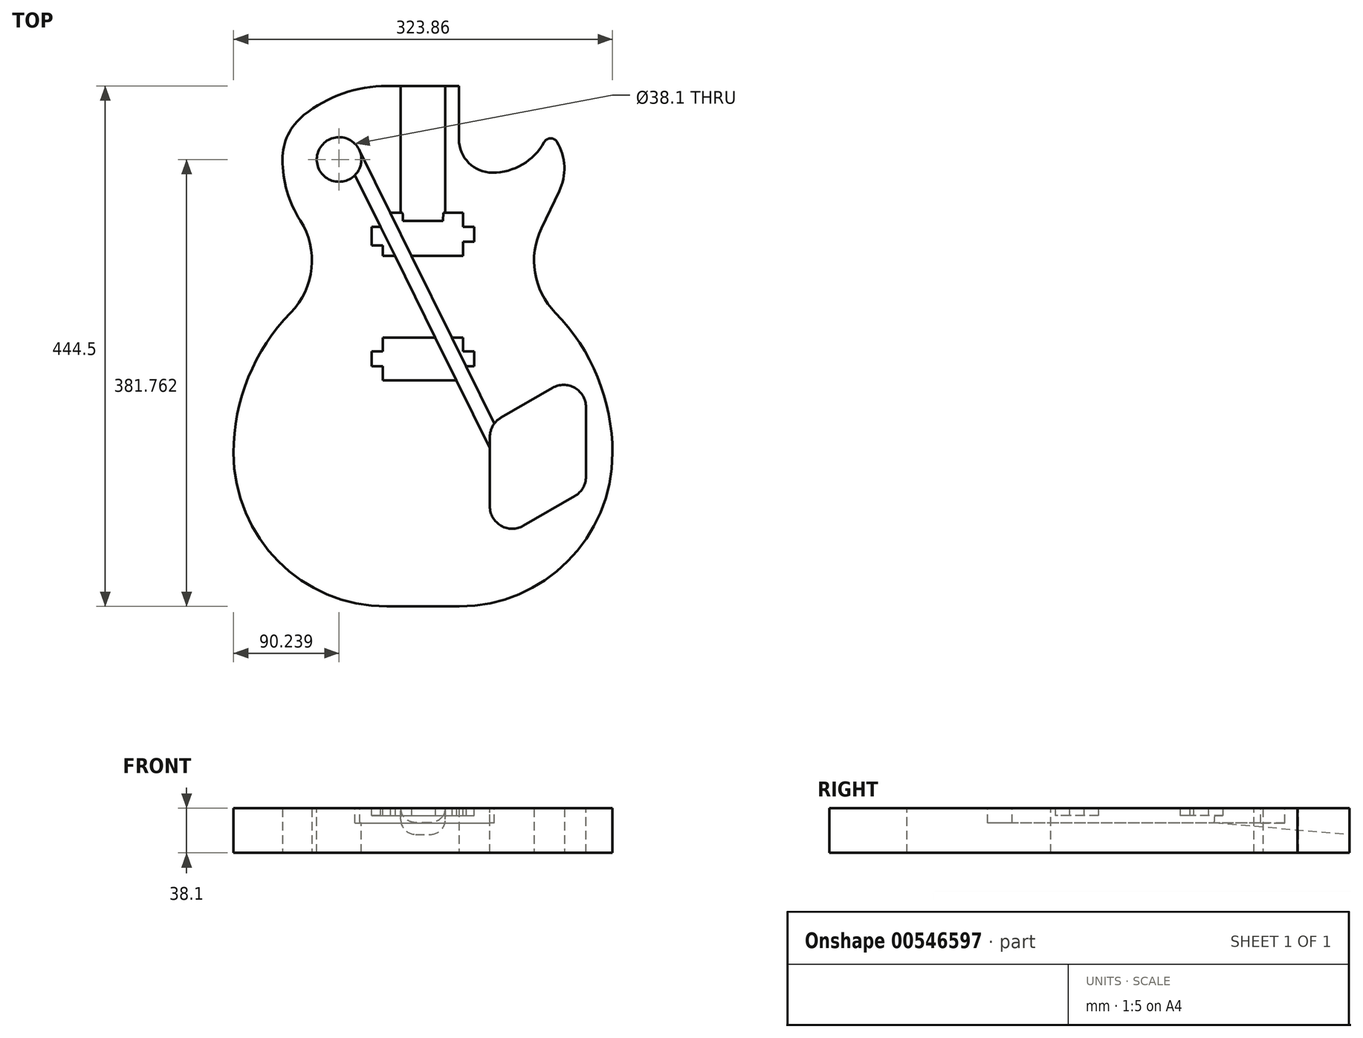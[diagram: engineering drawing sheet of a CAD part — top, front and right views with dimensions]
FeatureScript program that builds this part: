
annotation { "Feature Type Name" : "Feature", "Feature Type Description" : "" }
export const myFeature = defineFeature(function(context is Context, id is Id, definition is map)
    precondition{}
    {
        {
            var Q0;
            Q0=qCreatedBy(makeId("Top.planeOp"),FACE);
            var sketch = newSketch(context, id + "F0", { "sketchPlane" : qUnion([Q0])});
            skLineSegment(sketch, "E0.bottom", {"start": v(-161.92, 444.5) * mm, "end": v(161.92, 444.5) * mm});
            skLineSegment(sketch, "E0.top", {"start": v(-161.93, 0) * mm, "end": v(161.93, 0) * mm});
            skLineSegment(sketch, "E0.left", {"start": v(-161.92, 444.5) * mm, "end": v(-161.93, 0) * mm});
            skLineSegment(sketch, "E0.right", {"start": v(161.93, 444.5) * mm, "end": v(161.93, 0) * mm});
            skSolve(sketch);
        }
        {
            var Q0;
            Q0=qCreatedBy(makeId("Top.planeOp"),FACE);
            var sketch = newSketch(context, id + "F1", { "sketchPlane" : qUnion([Q0])});
            skLineSegment(sketch, "E1", {"start": v(-94.87, 295.4) * mm, "end": v(94.87, 295.4) * mm});
            skLineSegment(sketch, "E2", {"start": v(0, 0) * mm, "end": v(0, 295.4) * mm});
            skArc(sketch, "E3", {"start": v(-161.92, 131.02) * mm, "mid": v(-123.55, 38.37) * mm, "end": v(-30.9, 0) * mm});
            skLineSegment(sketch, "E4", {"start": v(-30.9, 0) * mm, "end": v(0, 0) * mm});
            skArc(sketch, "E5", {"start": v(-112.99, 250.99) * mm, "mid": v(-95.2, 288.9) * mm, "end": v(-104.89, 329.64) * mm});
            skLineSegment(sketch, "E6", {"start": v(-94.87, 295.4) * mm, "end": v(-94.87, 252.93) * mm});
            skLineSegment(sketch, "E7", {"start": v(-120.14, 381.76) * mm, "end": v(120.14, 381.76) * mm});
            skLineSegment(sketch, "E8", {"start": v(0, 295.4) * mm, "end": v(0, 381.76) * mm});
            skLineSegment(sketch, "E9", {"start": v(-120.14, 381.76) * mm, "end": v(-120.14, 343.59) * mm});
            skLineSegment(sketch, "E10", {"start": v(0, 381.76) * mm, "end": v(0, 444.5) * mm});
            skLineSegment(sketch, "E11", {"start": v(0, 444.5) * mm, "end": v(-30.73, 444.5) * mm});
            skArc(sketch, "E12", {"start": v(-112.99, 250.99) * mm, "mid": v(-149.22, 195.8) * mm, "end": v(-161.93, 131.02) * mm});
            skArc(sketch, "E13", {"start": v(-120.14, 381.76) * mm, "mid": v(-116.25, 354.6) * mm, "end": v(-104.89, 329.64) * mm});
            skArc(sketch, "E14", {"start": v(-101.83, 419.7) * mm, "mid": v(-115.32, 402.83) * mm, "end": v(-120.14, 381.76) * mm});
            skArc(sketch, "E15", {"start": v(-30.73, 444.5) * mm, "mid": v(-68.38, 438.12) * mm, "end": v(-101.83, 419.7) * mm});
            skLineSegment(sketch, "E16.MirrorCS", {"start": v(30.9, 0) * mm, "end": v(0, 0) * mm});
            skArc(sketch, "E17.MirrorCS", {"start": v(161.92, 131.02) * mm, "mid": v(123.55, 38.37) * mm, "end": v(30.9, 0) * mm});
            skArc(sketch, "E18.MirrorCS", {"start": v(112.99, 250.99) * mm, "mid": v(149.22, 195.8) * mm, "end": v(161.93, 131.02) * mm});
            skLineSegment(sketch, "E19", {"start": v(80.77, 399.8) * mm, "end": v(130.06, 399.8) * mm});
            skLineSegment(sketch, "E20", {"start": v(0, 444.5) * mm, "end": v(30.73, 444.5) * mm});
            skLineSegment(sketch, "E21", {"start": v(30.73, 444.5) * mm, "end": v(30.73, 399.03) * mm});
            skArc(sketch, "E22", {"start": v(30.73, 399.03) * mm, "mid": v(39.1, 378.83) * mm, "end": v(59.3, 370.46) * mm});
            skArc(sketch, "E23", {"start": v(101.18, 323) * mm, "mid": v(95.7, 285.13) * mm, "end": v(112.99, 250.99) * mm});
            skLineSegment(sketch, "E24", {"start": v(101.18, 323) * mm, "end": v(116.42, 354.6) * mm});
            skArc(sketch, "E25", {"start": v(116.42, 354.6) * mm, "mid": v(120.8, 375.88) * mm, "end": v(114.55, 396.7) * mm});
            skLineSegment(sketch, "E26", {"start": v(26.22, 370.46) * mm, "end": v(78.39, 370.46) * mm});
            skArc(sketch, "E27", {"start": v(114.55, 396.7) * mm, "mid": v(109, 399.8) * mm, "end": v(103.55, 396.52) * mm});
            skArc(sketch, "E28", {"start": v(59.3, 370.46) * mm, "mid": v(84.98, 377.46) * mm, "end": v(103.55, 396.52) * mm});
            skSolve(sketch);
        }
        {
            var Q0;
            {var subQ1=sQuery(id+"F1.wireOp",EDGE,"E10");Q0=makeQuery(id+"F1.imprint","IMPRINT",FACE,{"disambiguationData":[TD([[makeQuery(id+"F1.imprint","IMPRINT",EDGE,{"derivedFrom":subQ1}),1.0]])]});}
            var Q1;
            {var subQ1=sQuery(id+"F1.wireOp",EDGE,"E10");Q1=makeQuery(id+"F1.imprint","IMPRINT",FACE,{"disambiguationData":[TD([[makeQuery(id+"F1.imprint","IMPRINT",EDGE,{"derivedFrom":subQ1}),-1.0]])]});}
            var Q2;
            {var subQ5=sQuery(id+"F1.wireOp",EDGE,"E8");Q2=makeQuery(id+"F1.imprint","IMPRINT",FACE,{"disambiguationData":[TD([[makeQuery(id+"F1.imprint","IMPRINT",EDGE,{"derivedFrom":subQ5}),-1.0]])]});}
            var Q3;
            {var subQ0=sQuery(id+"F1.wireOp",EDGE,"E25");var subQ1=sQuery(id+"F1.wireOp",EDGE,"E7");var subQ2=makeQuery(id+"F1.imprint","INTERSECT",VERTEX,{"derivedFrom":[subQ1,subQ0]});Q3=makeQuery(id+"F1.imprint","IMPRINT",FACE,{"disambiguationData":[TD([[makeQuery(id+"F1.imprint","IMPRINT",EDGE,{"disambiguationData":[TD([[subQ2,1.0]])],"derivedFrom":subQ1}),1.0]])]});}
            var Q4;
            {var subQ0=sQuery(id+"F1.wireOp",EDGE,"E2");Q4=makeQuery(id+"F1.imprint","IMPRINT",FACE,{"disambiguationData":[TD([[makeQuery(id+"F1.imprint","IMPRINT",EDGE,{"derivedFrom":subQ0}),-1.0]])]});}
            var Q5;
            {var subQ1=sQuery(id+"F1.wireOp",EDGE,"E2");Q5=makeQuery(id+"F1.imprint","IMPRINT",FACE,{"disambiguationData":[TD([[makeQuery(id+"F1.imprint","IMPRINT",EDGE,{"derivedFrom":subQ1}),1.0]])]});}
            var Q6;
            {var subQ2=sQuery(id+"F1.wireOp",EDGE,"E8");Q6=makeQuery(id+"F1.imprint","IMPRINT",FACE,{"disambiguationData":[TD([[makeQuery(id+"F1.imprint","IMPRINT",EDGE,{"derivedFrom":subQ2}),1.0]])]});}
            extrude(context, id + "F2", {"entities" : qUnion([Q0, Q1, Q2, Q3, Q4, Q5, Q6]), "depth" : 38.1 * mm});
        }
        {
            var Q0;
            Q0=makeQuery(id+"F2.opExtrude","CAP_FACE",FACE,{"disambiguationData":[OSD([sQuery(id+"F1.wireOp",EDGE,"E3"),sQuery(id+"F1.wireOp",EDGE,"E4"),sQuery(id+"F1.wireOp",EDGE,"E5"),sQuery(id+"F1.wireOp",EDGE,"E11"),sQuery(id+"F1.wireOp",EDGE,"E12"),sQuery(id+"F1.wireOp",EDGE,"E13"),sQuery(id+"F1.wireOp",EDGE,"E14"),sQuery(id+"F1.wireOp",EDGE,"E15"),sQuery(id+"F1.wireOp",EDGE,"E16.MirrorCS"),sQuery(id+"F1.wireOp",EDGE,"E17.MirrorCS"),sQuery(id+"F1.wireOp",EDGE,"E18.MirrorCS"),sQuery(id+"F1.wireOp",EDGE,"E20"),sQuery(id+"F1.wireOp",EDGE,"E21"),sQuery(id+"F1.wireOp",EDGE,"E22"),sQuery(id+"F1.wireOp",EDGE,"E23"),sQuery(id+"F1.wireOp",EDGE,"E24"),sQuery(id+"F1.wireOp",EDGE,"E25"),sQuery(id+"F1.wireOp",EDGE,"E27"),sQuery(id+"F1.wireOp",EDGE,"E28")])],"isStart":false});
            var sketch = newSketch(context, id + "F3", { "sketchPlane" : qUnion([Q0])});
            skCircle(sketch, "E29", {"center": v(120.25, 170.1) * mm, "radius": 14.29 * mm});
            skCircle(sketch, "E30", {"center": v(76.2, 144.67) * mm, "radius": 14.29 * mm});
            skCircle(sketch, "E31", {"center": v(120.25, 110.8) * mm, "radius": 14.29 * mm});
            skCircle(sketch, "E32", {"center": v(76.2, 85.37) * mm, "radius": 14.29 * mm});
            skLineSegment(sketch, "E33", {"start": v(0, 0) * mm, "end": v(76.2, 144.67) * mm});
            skLineSegment(sketch, "E34", {"start": v(0, 0) * mm, "end": v(120.25, 110.8) * mm});
            skLineSegment(sketch, "E35", {"start": v(0, 0) * mm, "end": v(0, 365.77) * mm});
            skLineSegment(sketch, "E36", {"start": v(76.2, 144.67) * mm, "end": v(120.25, 110.8) * mm});
            skLineSegment(sketch, "E37", {"start": v(76.2, 144.67) * mm, "end": v(76.2, 85.37) * mm});
            skLineSegment(sketch, "E38", {"start": v(120.25, 110.8) * mm, "end": v(76.2, 85.37) * mm});
            skLineSegment(sketch, "E39", {"start": v(76.2, 144.67) * mm, "end": v(120.25, 170.1) * mm});
            skLineSegment(sketch, "E40", {"start": v(120.25, 110.8) * mm, "end": v(120.25, 170.1) * mm});
            skCircle(sketch, "E41", {"center": v(-71.7, 381.76) * mm, "radius": 19.05 * mm});
            skSolve(sketch);
        }
        {
            var Q0;
            Q0=makeQuery(id+"F3.imprint","IMPRINT",FACE,{"disambiguationData":[TD([[makeQuery(id+"F3.imprint","IMPRINT",EDGE,{"derivedFrom":sQuery(id+"F3.wireOp",EDGE,"E41")}),-1.0]])]});
            var sketch = newSketch(context, id + "F4", { "sketchPlane" : qUnion([Q0])});
            skCircle(sketch, "E42", {"center": v(-71.7, 381.76) * mm, "radius": 19.05 * mm});
            skArc(sketch, "E43", {"start": v(139.3, 170.1) * mm, "mid": v(129.77, 186.6) * mm, "end": v(110.72, 186.6) * mm});
            skArc(sketch, "E44", {"start": v(129.77, 94.3) * mm, "mid": v(136.74, 101.28) * mm, "end": v(139.3, 110.8) * mm});
            skArc(sketch, "E45", {"start": v(57.15, 85.37) * mm, "mid": v(66.67, 68.87) * mm, "end": v(85.72, 68.87) * mm});
            skArc(sketch, "E46", {"start": v(66.67, 161.17) * mm, "mid": v(59.7, 154.2) * mm, "end": v(57.15, 144.67) * mm});
            skLineSegment(sketch, "E47", {"start": v(110.72, 186.6) * mm, "end": v(66.68, 161.17) * mm});
            skLineSegment(sketch, "E48", {"start": v(57.15, 144.67) * mm, "end": v(57.15, 85.37) * mm});
            skLineSegment(sketch, "E49", {"start": v(85.72, 68.87) * mm, "end": v(129.77, 94.3) * mm});
            skLineSegment(sketch, "E50", {"start": v(139.3, 110.8) * mm, "end": v(139.3, 170.1) * mm});
            skSolve(sketch);
        }
        {
            var Q0;
            Q0=makeQuery(id+"F4.imprint","IMPRINT",FACE,{"disambiguationData":[TD([[makeQuery(id+"F4.imprint","IMPRINT",EDGE,{"derivedFrom":sQuery(id+"F4.wireOp",EDGE,"E42")}),1.0]])]});
            var Q1;
            Q1=makeQuery(id+"F4.imprint","IMPRINT",FACE,{"disambiguationData":[TD([[makeQuery(id+"F4.imprint","IMPRINT",EDGE,{"derivedFrom":sQuery(id+"F4.wireOp",EDGE,"E43")}),1.0]])]});
            var Q2;
            {var subQ1=sQuery(id+"F3.wireOp",EDGE,"E29");var subQ5=sQuery(id+"F3.wireOp",EDGE,"E39");var subQ6=makeQuery(id+"F3.imprint","INTERSECT",VERTEX,{"derivedFrom":[subQ1,subQ5]});Q2=makeQuery(id+"F4.imprint","IMPRINT",FACE,{"disambiguationData":[TD([[makeQuery(id+"F4.imprint","IMPRINT",EDGE,{"derivedFrom":makeQuery(id+"F3.imprint","IMPRINT",EDGE,{"disambiguationData":[TD([[subQ6,1.0]])],"derivedFrom":subQ1})}),1.0]])]});}
            extrude(context, id + "F5", {"entities" : qUnion([Q0, Q1, Q2]), "operationType" : NewBodyOperationType.REMOVE, "endBound" : BoundingType.THROUGH_ALL, "oppositeDirection" : true, "depth" : 25.4 * mm});
        }
        {
            var Q0;
            Q0=makeQuery(id+"F2.opExtrude","CAP_FACE",FACE,{"disambiguationData":[OSD([sQuery(id+"F1.wireOp",EDGE,"E3"),sQuery(id+"F1.wireOp",EDGE,"E4"),sQuery(id+"F1.wireOp",EDGE,"E5"),sQuery(id+"F1.wireOp",EDGE,"E11"),sQuery(id+"F1.wireOp",EDGE,"E12"),sQuery(id+"F1.wireOp",EDGE,"E13"),sQuery(id+"F1.wireOp",EDGE,"E14"),sQuery(id+"F1.wireOp",EDGE,"E15"),sQuery(id+"F1.wireOp",EDGE,"E16.MirrorCS"),sQuery(id+"F1.wireOp",EDGE,"E17.MirrorCS"),sQuery(id+"F1.wireOp",EDGE,"E18.MirrorCS"),sQuery(id+"F1.wireOp",EDGE,"E20"),sQuery(id+"F1.wireOp",EDGE,"E21"),sQuery(id+"F1.wireOp",EDGE,"E22"),sQuery(id+"F1.wireOp",EDGE,"E23"),sQuery(id+"F1.wireOp",EDGE,"E24"),sQuery(id+"F1.wireOp",EDGE,"E25"),sQuery(id+"F1.wireOp",EDGE,"E27"),sQuery(id+"F1.wireOp",EDGE,"E28")])],"isStart":false});
            var sketch = newSketch(context, id + "F6", { "sketchPlane" : qUnion([Q0])});
            skArc(sketch, "E51", {"start": v(-69.5, 374.93) * mm, "mid": v(-78.43, 375.8) * mm, "end": v(-79.3, 366.85) * mm});
            skArc(sketch, "E52", {"start": v(90.35, 161.06) * mm, "mid": v(99.29, 160.2) * mm, "end": v(100.15, 169.14) * mm});
            skLineSegment(sketch, "E53", {"start": v(90.35, 161.06) * mm, "end": v(-79.3, 366.85) * mm});
            skLineSegment(sketch, "E54", {"start": v(-69.5, 374.93) * mm, "end": v(100.15, 169.14) * mm});
            skLineSegment(sketch, "E55", {"start": v(0, 0) * mm, "end": v(0, 165.1) * mm});
            skLineSegment(sketch, "E56", {"start": v(0, 165.1) * mm, "end": v(95.25, 165.1) * mm});
            skSolve(sketch);
        }
        {
            var Q0;
            {var subQ0=sQuery(id+"F6.wireOp",EDGE,"E53");var subQ1=makeQuery(id+"F5.boolean.opBoolean","COPY",EDGE,{"derivedFrom":makeQuery(id+"F5.opExtrude","CAP_EDGE",EDGE,{"disambiguationData":[OSD([sQuery(id+"F4.wireOp",EDGE,"MkLr8Pz1-1iLs-kMEC-wIaN-vfKRpLqlfBYC")])],"isStart":true})});var subQ2=makeQuery(id+"F6.imprint","INTERSECT",VERTEX,{"derivedFrom":[subQ1,subQ0]});Q0=makeQuery(id+"F6.imprint","IMPRINT",FACE,{"disambiguationData":[TD([[makeQuery(id+"F6.imprint","IMPRINT",EDGE,{"disambiguationData":[TD([[subQ2,-1.0]])],"derivedFrom":subQ0}),-1.0]])]});}
            extrude(context, id + "F7", {"entities" : qUnion([Q0]), "operationType" : NewBodyOperationType.REMOVE, "oppositeDirection" : true, "depth" : 12.7 * mm});
        }
        {
            var Q0;
            Q0=makeQuery(id+"F2.opExtrude","SWEPT_FACE",FACE,{"disambiguationData":[OSD([sQuery(id+"F1.wireOp",EDGE,"E21")])]});
            var sketch = newSketch(context, id + "F8", { "sketchPlane" : qUnion([Q0])});
            skLineSegment(sketch, "E57", {"start": v(444.5, 0) * mm, "end": v(451.24, 77) * mm});
            skSolve(sketch);
        }
        {
            var Q0;
            Q0=makeQuery(id+"F2.opExtrude","CAP_EDGE",EDGE,{"disambiguationData":[OSD([sQuery(id+"F1.wireOp",EDGE,"E11"),sQuery(id+"F1.wireOp",EDGE,"E20")])],"isStart":true});
            var Q1;
            Q1=sQuery(id+"F8.wireOp",EDGE,"E57");
            cPlane(context, id + "F9", {"entities" : qUnion([Q0, Q1]), "cplaneType" : CPlaneType.LINE_ANGLE, "offset" : 25.4 * mm, "angle" : 0 * degree, "width" : 152.4 * mm, "height" : 152.4 * mm});
        }
        {
            var Q0;
            Q0=qCreatedBy(id+"F9.planeOp",FACE);
            var sketch = newSketch(context, id + "F10", { "sketchPlane" : qUnion([Q0])});
            skLineSegment(sketch, "E58", {"start": v(-19.05, 76.7) * mm, "end": v(19.05, 76.7) * mm});
            skLineSegment(sketch, "E59", {"start": v(19.05, 76.7) * mm, "end": v(19.05, 67.17) * mm});
            skLineSegment(sketch, "E60", {"start": v(-19.05, 76.7) * mm, "end": v(-19.05, 67.17) * mm});
            skLineSegment(sketch, "E61", {"start": v(-6.35, 54.47) * mm, "end": v(6.35, 54.47) * mm});
            skArc(sketch, "E62", {"start": v(-19.05, 67.17) * mm, "mid": v(-15.33, 58.2) * mm, "end": v(-6.35, 54.47) * mm});
            skArc(sketch, "E63", {"start": v(6.35, 54.47) * mm, "mid": v(15.33, 58.2) * mm, "end": v(19.05, 67.17) * mm});
            skLineSegment(sketch, "E64", {"start": v(0, 38.74) * mm, "end": v(0, 54.47) * mm});
            skSolve(sketch);
        }
        {
            var Q0;
            Q0=qSketchRegion(id+"F10",true);
            extrude(context, id + "F11", {"entities" : qUnion([Q0]), "operationType" : NewBodyOperationType.REMOVE, "oppositeDirection" : true, "depth" : 117.47 * mm});
        }
        {
            var Q0;
            Q0=makeQuery(id+"F2.opExtrude","CAP_FACE",FACE,{"disambiguationData":[OSD([sQuery(id+"F1.wireOp",EDGE,"E3"),sQuery(id+"F1.wireOp",EDGE,"E4"),sQuery(id+"F1.wireOp",EDGE,"E5"),sQuery(id+"F1.wireOp",EDGE,"E11"),sQuery(id+"F1.wireOp",EDGE,"E12"),sQuery(id+"F1.wireOp",EDGE,"E13"),sQuery(id+"F1.wireOp",EDGE,"E14"),sQuery(id+"F1.wireOp",EDGE,"E15"),sQuery(id+"F1.wireOp",EDGE,"E16.MirrorCS"),sQuery(id+"F1.wireOp",EDGE,"E17.MirrorCS"),sQuery(id+"F1.wireOp",EDGE,"E18.MirrorCS"),sQuery(id+"F1.wireOp",EDGE,"E20"),sQuery(id+"F1.wireOp",EDGE,"E21"),sQuery(id+"F1.wireOp",EDGE,"E22"),sQuery(id+"F1.wireOp",EDGE,"E23"),sQuery(id+"F1.wireOp",EDGE,"E24"),sQuery(id+"F1.wireOp",EDGE,"E25"),sQuery(id+"F1.wireOp",EDGE,"E27"),sQuery(id+"F1.wireOp",EDGE,"E28")])],"isStart":false});
            var sketch = newSketch(context, id + "F12", { "sketchPlane" : qUnion([Q0])});
            skLineSegment(sketch, "E65.bottom", {"start": v(-34.3, 229.67) * mm, "end": v(34.3, 229.67) * mm});
            skLineSegment(sketch, "E65.top", {"start": v(-34.3, 193.04) * mm, "end": v(34.29, 193.04) * mm});
            skLineSegment(sketch, "E65.left", {"start": v(-34.3, 229.67) * mm, "end": v(-34.3, 193.04) * mm});
            skLineSegment(sketch, "E65.right", {"start": v(34.3, 229.67) * mm, "end": v(34.3, 193.04) * mm});
            skLineSegment(sketch, "E66.bottom", {"start": v(-34.3, 336.14) * mm, "end": v(34.29, 336.14) * mm});
            skLineSegment(sketch, "E66.top", {"start": v(-34.3, 299.52) * mm, "end": v(34.29, 299.52) * mm});
            skLineSegment(sketch, "E66.left", {"start": v(-34.3, 336.14) * mm, "end": v(-34.3, 299.52) * mm});
            skLineSegment(sketch, "E66.right", {"start": v(34.29, 336.14) * mm, "end": v(34.29, 299.52) * mm});
            skLineSegment(sketch, "E67", {"start": v(0, 444.5) * mm, "end": v(0, 336.14) * mm});
            skLineSegment(sketch, "E68", {"start": v(0, 299.52) * mm, "end": v(0, 229.67) * mm});
            skLineSegment(sketch, "E69", {"start": v(0, 229.67) * mm, "end": v(0, 211.35) * mm});
            skLineSegment(sketch, "E70", {"start": v(0, 211.35) * mm, "end": v(0, 193.04) * mm});
            skLineSegment(sketch, "E71.bottom", {"start": v(-34.3, 324.18) * mm, "end": v(-43.82, 324.18) * mm});
            skLineSegment(sketch, "E71.left", {"start": v(-34.3, 324.18) * mm, "end": v(-34.3, 311.48) * mm});
            skLineSegment(sketch, "E71.right", {"start": v(-43.82, 324.18) * mm, "end": v(-43.82, 311.48) * mm});
            skLineSegment(sketch, "E72.bottom", {"start": v(34.29, 324.18) * mm, "end": v(43.81, 324.18) * mm});
            skLineSegment(sketch, "E72.top", {"start": v(34.29, 311.48) * mm, "end": v(43.81, 311.48) * mm});
            skLineSegment(sketch, "E72.left", {"start": v(34.29, 324.18) * mm, "end": v(34.29, 311.48) * mm});
            skLineSegment(sketch, "E72.right", {"start": v(43.81, 324.18) * mm, "end": v(43.81, 311.48) * mm});
            skLineSegment(sketch, "E73.bottom", {"start": v(34.3, 217.7) * mm, "end": v(43.82, 217.7) * mm});
            skLineSegment(sketch, "E73.top", {"start": v(34.3, 205) * mm, "end": v(43.82, 205) * mm});
            skLineSegment(sketch, "E73.left", {"start": v(34.3, 217.7) * mm, "end": v(34.3, 205) * mm});
            skLineSegment(sketch, "E73.right", {"start": v(43.82, 217.7) * mm, "end": v(43.82, 205) * mm});
            skLineSegment(sketch, "E74.bottom", {"start": v(-34.3, 205) * mm, "end": v(-43.82, 205) * mm});
            skLineSegment(sketch, "E74.top", {"start": v(-34.3, 217.7) * mm, "end": v(-43.82, 217.7) * mm});
            skLineSegment(sketch, "E74.left", {"start": v(-34.3, 205) * mm, "end": v(-34.3, 217.7) * mm});
            skLineSegment(sketch, "E74.right", {"start": v(-43.82, 205) * mm, "end": v(-43.82, 217.7) * mm});
            skLineSegment(sketch, "E75", {"start": v(-43.82, 211.35) * mm, "end": v(0, 211.35) * mm});
            skLineSegment(sketch, "E76", {"start": v(43.82, 211.35) * mm, "end": v(0, 211.35) * mm});
            skLineSegment(sketch, "E77", {"start": v(43.81, 317.83) * mm, "end": v(0, 317.83) * mm});
            skLineSegment(sketch, "E78", {"start": v(-43.82, 317.83) * mm, "end": v(0, 317.83) * mm});
            skLineSegment(sketch, "E79", {"start": v(-43.82, 311.48) * mm, "end": v(-43.82, 308.3) * mm});
            skLineSegment(sketch, "E80", {"start": v(-43.82, 308.3) * mm, "end": v(-34.3, 308.3) * mm});
            skLineSegment(sketch, "E81", {"start": v(0, 299.52) * mm, "end": v(0, 317.83) * mm});
            skLineSegment(sketch, "E82", {"start": v(0, 336.14) * mm, "end": v(0, 317.83) * mm});
            skSolve(sketch);
        }
        {
            var Q0;
            Q0=qSketchRegion(id+"F12",true);
            extrude(context, id + "F13", {"entities" : qUnion([Q0]), "operationType" : NewBodyOperationType.REMOVE, "oppositeDirection" : true, "depth" : 6.35 * mm});
        }
        {
            var Q0;
            Q0=makeQuery(id+"F2.opExtrude","CAP_FACE",FACE,{"disambiguationData":[OSD([sQuery(id+"F1.wireOp",EDGE,"E3"),sQuery(id+"F1.wireOp",EDGE,"E4"),sQuery(id+"F1.wireOp",EDGE,"E5"),sQuery(id+"F1.wireOp",EDGE,"E11"),sQuery(id+"F1.wireOp",EDGE,"E12"),sQuery(id+"F1.wireOp",EDGE,"E13"),sQuery(id+"F1.wireOp",EDGE,"E14"),sQuery(id+"F1.wireOp",EDGE,"E15"),sQuery(id+"F1.wireOp",EDGE,"E16.MirrorCS"),sQuery(id+"F1.wireOp",EDGE,"E17.MirrorCS"),sQuery(id+"F1.wireOp",EDGE,"E18.MirrorCS"),sQuery(id+"F1.wireOp",EDGE,"E20"),sQuery(id+"F1.wireOp",EDGE,"E21"),sQuery(id+"F1.wireOp",EDGE,"E22"),sQuery(id+"F1.wireOp",EDGE,"E23"),sQuery(id+"F1.wireOp",EDGE,"E24"),sQuery(id+"F1.wireOp",EDGE,"E25"),sQuery(id+"F1.wireOp",EDGE,"E27"),sQuery(id+"F1.wireOp",EDGE,"E28")])],"isStart":false});
            var sketch = newSketch(context, id + "F14", { "sketchPlane" : qUnion([Q0])});
            skLineSegment(sketch, "E83", {"start": v(-58.08, 368.44) * mm, "end": v(57.15, 135.25) * mm});
            skLineSegment(sketch, "E84", {"start": v(-54.07, 389) * mm, "end": v(61, 156.15) * mm});
            skLineSegment(sketch, "E85", {"start": v(-58.08, 368.44) * mm, "end": v(-54.07, 389) * mm});
            skLineSegment(sketch, "E86", {"start": v(57.15, 135.26) * mm, "end": v(57.15, 144.67) * mm});
            skArc(sketch, "E87", {"start": v(61, 156.15) * mm, "mid": v(58.14, 150.72) * mm, "end": v(57.15, 144.67) * mm});
            skSolve(sketch);
        }
        {
            var Q0;
            Q0=qSketchRegion(id+"F14",true);
            extrude(context, id + "F15", {"entities" : qUnion([Q0]), "operationType" : NewBodyOperationType.REMOVE, "oppositeDirection" : true, "depth" : 12.7 * mm});
        }
    });
